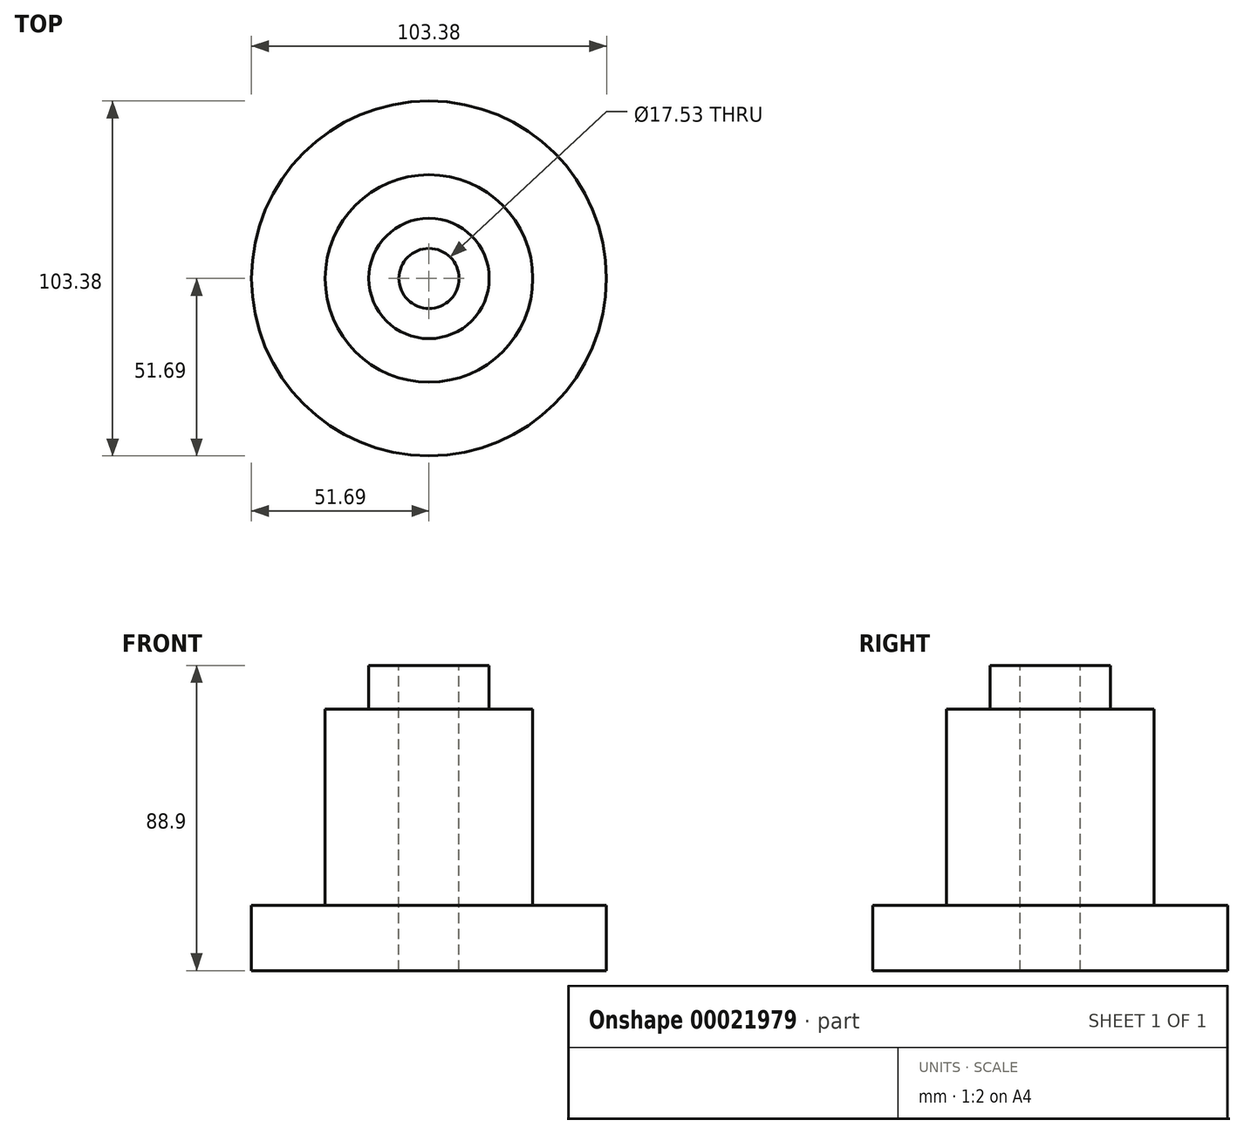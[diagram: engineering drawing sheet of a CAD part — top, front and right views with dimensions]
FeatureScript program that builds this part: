
annotation { "Feature Type Name" : "Feature", "Feature Type Description" : "" }
export const myFeature = defineFeature(function(context is Context, id is Id, definition is map)
    precondition{}
    {
        {
            var Q0;
            Q0=qCreatedBy(makeId("Front.planeOp"),FACE);
            var sketch = newSketch(context, id + "F0", { "sketchPlane" : qUnion([Q0])});
            skLineSegment(sketch, "E0.bottom", {"start": v(-51.69, 14.84) * mm, "end": v(-30.23, 14.84) * mm});
            skLineSegment(sketch, "E0.top", {"start": v(-51.69, -4.2) * mm, "end": v(-30.23, -4.2) * mm});
            skLineSegment(sketch, "E0.left", {"start": v(-51.69, 14.84) * mm, "end": v(-51.69, -4.2) * mm});
            skLineSegment(sketch, "E1.bottom", {"start": v(-30.23, -4.2) * mm, "end": v(-27.81, -4.2) * mm});
            skLineSegment(sketch, "E1.top", {"start": v(-30.23, 72) * mm, "end": v(-17.53, 72) * mm});
            skLineSegment(sketch, "E1.left", {"start": v(-30.23, 14.84) * mm, "end": v(-30.23, 72) * mm});
            skLineSegment(sketch, "E2.bottom", {"start": v(-27.81, -4.2) * mm, "end": v(-8.76, -4.2) * mm});
            skLineSegment(sketch, "E2.top", {"start": v(-17.53, 84.7) * mm, "end": v(-8.76, 84.7) * mm});
            skLineSegment(sketch, "E2.right", {"start": v(-8.76, -4.2) * mm, "end": v(-8.76, 84.7) * mm});
            skLineSegment(sketch, "E3", {"start": v(0, 132.69) * mm, "end": v(0, -69.78) * mm});
            skLineSegment(sketch, "E4", {"start": v(-17.53, 84.7) * mm, "end": v(-17.53, 72) * mm});
            skSolve(sketch);
        }
        {
            var Q0;
            {var subQ2=sQuery(id+"F0.wireOp",EDGE,"E1.bottom");Q0=makeQuery(id+"F0.imprint","IMPRINT",FACE,{"disambiguationData":[TD([[makeQuery(id+"F0.imprint","IMPRINT",EDGE,{"derivedFrom":subQ2}),1.0]])]});}
            var Q1;
            {var subQ3=sQuery(id+"F0.wireOp",EDGE,"E2.bottom");Q1=makeQuery(id+"F0.imprint","IMPRINT",FACE,{"disambiguationData":[TD([[makeQuery(id+"F0.imprint","IMPRINT",EDGE,{"derivedFrom":subQ3}),1.0]])]});}
            var Q2;
            {var subQ2=sQuery(id+"F0.wireOp",EDGE,"E0.bottom");Q2=makeQuery(id+"F0.imprint","IMPRINT",FACE,{"disambiguationData":[TD([[makeQuery(id+"F0.imprint","IMPRINT",EDGE,{"derivedFrom":subQ2}),-1.0]])]});}
            var Q3;
            Q3=sQuery(id+"F0.wireOp",EDGE,"E3");
            revolve(context, id + "F1", {"entities" : qUnion([Q0, Q1, Q2]), "axis" : qUnion([Q3]), "revolveType" : RevolveType.FULL});
        }
    });
